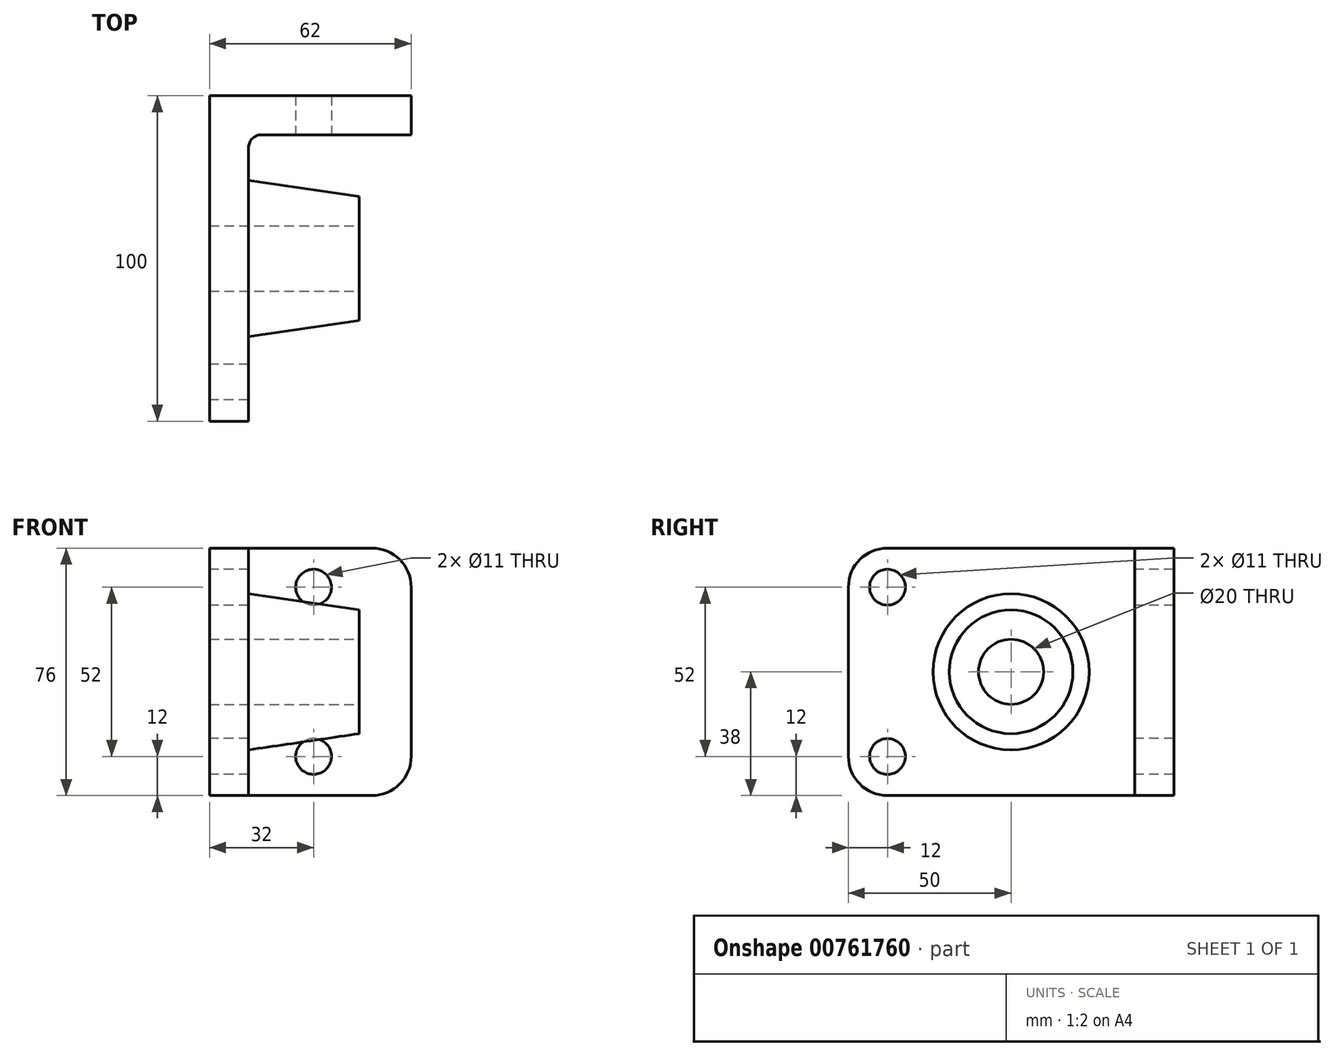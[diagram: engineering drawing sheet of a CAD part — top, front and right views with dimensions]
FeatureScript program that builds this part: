
annotation { "Feature Type Name" : "Feature", "Feature Type Description" : "" }
export const myFeature = defineFeature(function(context is Context, id is Id, definition is map)
    precondition{}
    {
        {
            var Q0;
            Q0=qCreatedBy(makeId("Right.planeOp"),FACE);
            var sketch = newSketch(context, id + "F0", { "sketchPlane" : qUnion([Q0])});
            skLineSegment(sketch, "E0.bottom", {"start": v(12, 0) * mm, "end": v(100, 0) * mm});
            skLineSegment(sketch, "E0.top", {"start": v(12, 76) * mm, "end": v(100, 76) * mm});
            skLineSegment(sketch, "E0.left", {"start": v(0, 12) * mm, "end": v(0, 64) * mm});
            skLineSegment(sketch, "E0.right", {"start": v(100, 0) * mm, "end": v(100, 76) * mm});
            skPoint(sketch, "E1.visualSharp", {"position": v(0, 76) * mm});
            skArc(sketch, "E1.filletArc", {"start": v(12, 76) * mm, "mid": v(3.51, 72.49) * mm, "end": v(0, 64) * mm});
            skPoint(sketch, "E2.visualSharp", {"position": v(0, 0) * mm});
            skArc(sketch, "E2.filletArc", {"start": v(0, 12) * mm, "mid": v(3.51, 3.51) * mm, "end": v(12, 0) * mm});
            skCircle(sketch, "E3", {"center": v(12, 64) * mm, "radius": 5.5 * mm});
            skCircle(sketch, "E4", {"center": v(12, 12) * mm, "radius": 5.5 * mm});
            skSolve(sketch);
        }
        {
            var Q0;
            Q0=makeQuery(id+"F0.imprint","IMPRINT",FACE,{"disambiguationData":[TD([[makeQuery(id+"F0.imprint","IMPRINT",EDGE,{"derivedFrom":sQuery(id+"F0.wireOp",EDGE,"E0.bottom")}),1.0]])]});
            extrude(context, id + "F1", {"entities" : qUnion([Q0]), "depth" : 12 * mm, "offsetDistance" : 25 * mm});
        }
        {
            var Q0;
            Q0=makeQuery(id+"F1.opExtrude","CAP_FACE",FACE,{"disambiguationData":[OSD([sQuery(id+"F0.wireOp",EDGE,"E0.bottom"),sQuery(id+"F0.wireOp",EDGE,"E0.top"),sQuery(id+"F0.wireOp",EDGE,"E0.left"),sQuery(id+"F0.wireOp",EDGE,"E0.right"),sQuery(id+"F0.wireOp",EDGE,"E1.filletArc"),sQuery(id+"F0.wireOp",EDGE,"E2.filletArc"),sQuery(id+"F0.wireOp",EDGE,"E3"),sQuery(id+"F0.wireOp",EDGE,"E4")])],"isStart":false});
            var sketch = newSketch(context, id + "F2", { "sketchPlane" : qUnion([Q0])});
            skLineSegment(sketch, "E5", {"start": v(100, 76) * mm, "end": v(88, 76) * mm});
            skLineSegment(sketch, "E6", {"start": v(88, 76) * mm, "end": v(88, 0) * mm});
            skLineSegment(sketch, "E7", {"start": v(88, 0) * mm, "end": v(100, 0) * mm});
            skLineSegment(sketch, "E8", {"start": v(100, 0) * mm, "end": v(100, 76) * mm});
            skSolve(sketch);
        }
        {
            var Q0;
            Q0=makeQuery(id+"F2.imprint","IMPRINT",FACE,{"disambiguationData":[TD([[makeQuery(id+"F2.imprint","IMPRINT",EDGE,{"derivedFrom":sQuery(id+"F2.wireOp",EDGE,"E5")}),-1.0]])]});
            extrude(context, id + "F3", {"entities" : qUnion([Q0]), "operationType" : NewBodyOperationType.ADD, "depth" : 50 * mm, "offsetDistance" : 25 * mm});
        }
        {
            var Q0;
            Q0=makeQuery(id+"F3.opExtrude","SWEPT_FACE",FACE,{"disambiguationData":[OSD([sQuery(id+"F2.wireOp",EDGE,"E6")])]});
            var sketch = newSketch(context, id + "F4", { "sketchPlane" : qUnion([Q0])});
            skCircle(sketch, "E9", {"center": v(32, 64) * mm, "radius": 5.5 * mm});
            skCircle(sketch, "E10", {"center": v(32, 12) * mm, "radius": 5.5 * mm});
            skLineSegment(sketch, "E11", {"start": v(62, 64) * mm, "end": v(62, 12) * mm});
            skPoint(sketch, "E12.visualSharp", {"position": v(62, 76) * mm});
            skArc(sketch, "E12.filletArc", {"start": v(62, 64) * mm, "mid": v(58.49, 72.49) * mm, "end": v(50, 76) * mm});
            skPoint(sketch, "E13.visualSharp", {"position": v(62, 0) * mm});
            skArc(sketch, "E13.filletArc", {"start": v(50, 0) * mm, "mid": v(58.49, 3.51) * mm, "end": v(62, 12) * mm});
            skLineSegment(sketch, "E14", {"start": v(50, 0) * mm, "end": v(62, 0) * mm});
            skLineSegment(sketch, "E15", {"start": v(62, 76) * mm, "end": v(50, 76) * mm});
            skSolve(sketch);
        }
        {
            var Q0;
            Q0=makeQuery(id+"F4.imprint","IMPRINT",FACE,{"disambiguationData":[TD([[makeQuery(id+"F4.imprint","IMPRINT",EDGE,{"derivedFrom":sQuery(id+"F4.wireOp",EDGE,"E9")}),1.0]])]});
            var Q1;
            Q1=makeQuery(id+"F4.imprint","IMPRINT",FACE,{"disambiguationData":[TD([[makeQuery(id+"F4.imprint","IMPRINT",EDGE,{"derivedFrom":sQuery(id+"F4.wireOp",EDGE,"E10")}),1.0]])]});
            var Q2;
            {var subQ0=sQuery(id+"F4.wireOp",EDGE,"E12.filletArc");Q2=makeQuery(id+"F4.imprint","IMPRINT",FACE,{"disambiguationData":[TD([[makeQuery(id+"F4.imprint","IMPRINT",EDGE,{"derivedFrom":subQ0}),-1.0]])]});}
            var Q3;
            {var subQ0=sQuery(id+"F4.wireOp",EDGE,"E13.filletArc");Q3=makeQuery(id+"F4.imprint","IMPRINT",FACE,{"disambiguationData":[TD([[makeQuery(id+"F4.imprint","IMPRINT",EDGE,{"derivedFrom":subQ0}),-1.0]])]});}
            extrude(context, id + "F5", {"entities" : qUnion([Q0, Q1, Q2, Q3]), "operationType" : NewBodyOperationType.REMOVE, "oppositeDirection" : true, "depth" : 12 * mm, "offsetDistance" : 25 * mm});
        }
        {
            var Q0;
            Q0=makeQuery(id+"F1.opExtrude","CAP_FACE",FACE,{"disambiguationData":[OSD([sQuery(id+"F0.wireOp",EDGE,"E0.bottom"),sQuery(id+"F0.wireOp",EDGE,"E0.top"),sQuery(id+"F0.wireOp",EDGE,"E0.left"),sQuery(id+"F0.wireOp",EDGE,"E0.right"),sQuery(id+"F0.wireOp",EDGE,"E1.filletArc"),sQuery(id+"F0.wireOp",EDGE,"E2.filletArc"),sQuery(id+"F0.wireOp",EDGE,"E3"),sQuery(id+"F0.wireOp",EDGE,"E4")])],"isStart":false});
            var sketch = newSketch(context, id + "F6", { "sketchPlane" : qUnion([Q0])});
            skCircle(sketch, "E16", {"center": v(50, 38) * mm, "radius": 24 * mm});
            skSolve(sketch);
        }
        {
            var Q0;
            Q0=makeQuery(id+"F6.imprint","IMPRINT",FACE,{"disambiguationData":[TD([[makeQuery(id+"F6.imprint","IMPRINT",EDGE,{"derivedFrom":sQuery(id+"F6.wireOp",EDGE,"E16")}),-1.0]])]});
            cPlane(context, id + "F7", {"entities" : qUnion([Q0]), "cplaneType" : CPlaneType.OFFSET, "offset" : 34 * mm, "width" : 150 * mm, "height" : 150 * mm});
        }
        {
            var Q0;
            Q0=qCreatedBy(id+"F7.planeOp",FACE);
            var sketch = newSketch(context, id + "F8", { "sketchPlane" : qUnion([Q0])});
            skCircle(sketch, "E17", {"center": v(50, 38) * mm, "radius": 19 * mm});
            skSolve(sketch);
        }
        {
            var Q1;
            Q1=makeQuery(id+"F8.imprint","IMPRINT",FACE,{"disambiguationData":[TD([[makeQuery(id+"F8.imprint","IMPRINT",EDGE,{"derivedFrom":sQuery(id+"F8.wireOp",EDGE,"E17")}),1.0]])]});
            var Q2;
            Q2=makeQuery(id+"F6.imprint","IMPRINT",FACE,{"disambiguationData":[TD([[makeQuery(id+"F6.imprint","IMPRINT",EDGE,{"derivedFrom":sQuery(id+"F6.wireOp",EDGE,"E16")}),1.0]])]});
            loft(context, id + "F9", {"operationType" : NewBodyOperationType.ADD, "sheetProfilesArray" : [{ "sheetProfileEntities" : qUnion([Q1]) }, { "sheetProfileEntities" : qUnion([Q2]) }]});
        }
        {
            var Q0;
            Q0=makeQuery(id+"F9.opLoft","CAP_FACE",FACE,{"disambiguationData":[OSD([makeQuery(id+"F8.imprint","IMPRINT",FACE,{"disambiguationData":[TD([[makeQuery(id+"F8.imprint","IMPRINT",EDGE,{"derivedFrom":sQuery(id+"F8.wireOp",EDGE,"E17")}),1.0]])]})])],"isStart":true});
            var sketch = newSketch(context, id + "F10", { "sketchPlane" : qUnion([Q0])});
            skCircle(sketch, "E18", {"center": v(50, 38) * mm, "radius": 10 * mm});
            skSolve(sketch);
        }
        {
            var Q0;
            Q0=makeQuery(id+"F10.imprint","IMPRINT",FACE,{"disambiguationData":[TD([[makeQuery(id+"F10.imprint","IMPRINT",EDGE,{"derivedFrom":sQuery(id+"F10.wireOp",EDGE,"E18")}),1.0]])]});
            extrude(context, id + "F11", {"entities" : qUnion([Q0]), "operationType" : NewBodyOperationType.REMOVE, "oppositeDirection" : true, "depth" : 46 * mm, "offsetDistance" : 25 * mm});
        }
        {
            var Q0;
            Q0=makeQuery(id+"F3.boolean.opBoolean","MERGE",FACE,{"derivedFrom":[makeQuery(id+"F1.opExtrude","SWEPT_FACE",FACE,{"disambiguationData":[OSD([sQuery(id+"F0.wireOp",EDGE,"E0.top")])]}),makeQuery(id+"F3.opExtrude","SWEPT_FACE",FACE,{"disambiguationData":[OSD([sQuery(id+"F2.wireOp",EDGE,"E5")])]})]});
            var sketch = newSketch(context, id + "F12", { "sketchPlane" : qUnion([Q0])});
            skPoint(sketch, "E19.visualSharp", {"position": v(12, 88) * mm});
            skArc(sketch, "E19.filletArc", {"start": v(16, 88) * mm, "mid": v(13.17, 86.83) * mm, "end": v(12, 84) * mm});
            skLineSegment(sketch, "E20", {"start": v(12, 84) * mm, "end": v(12, 88) * mm});
            skSolve(sketch);
        }
        {
            var Q0;
            {var subQ0=sQuery(id+"F12.wireOp",EDGE,"E19.filletArc");Q0=makeQuery(id+"F12.imprint","IMPRINT",FACE,{"disambiguationData":[TD([[makeQuery(id+"F12.imprint","IMPRINT",EDGE,{"derivedFrom":subQ0}),-1.0]])]});}
            extrude(context, id + "F13", {"entities" : qUnion([Q0]), "operationType" : NewBodyOperationType.ADD, "oppositeDirection" : true, "depth" : 76 * mm, "offsetDistance" : 25 * mm});
        }
    });
